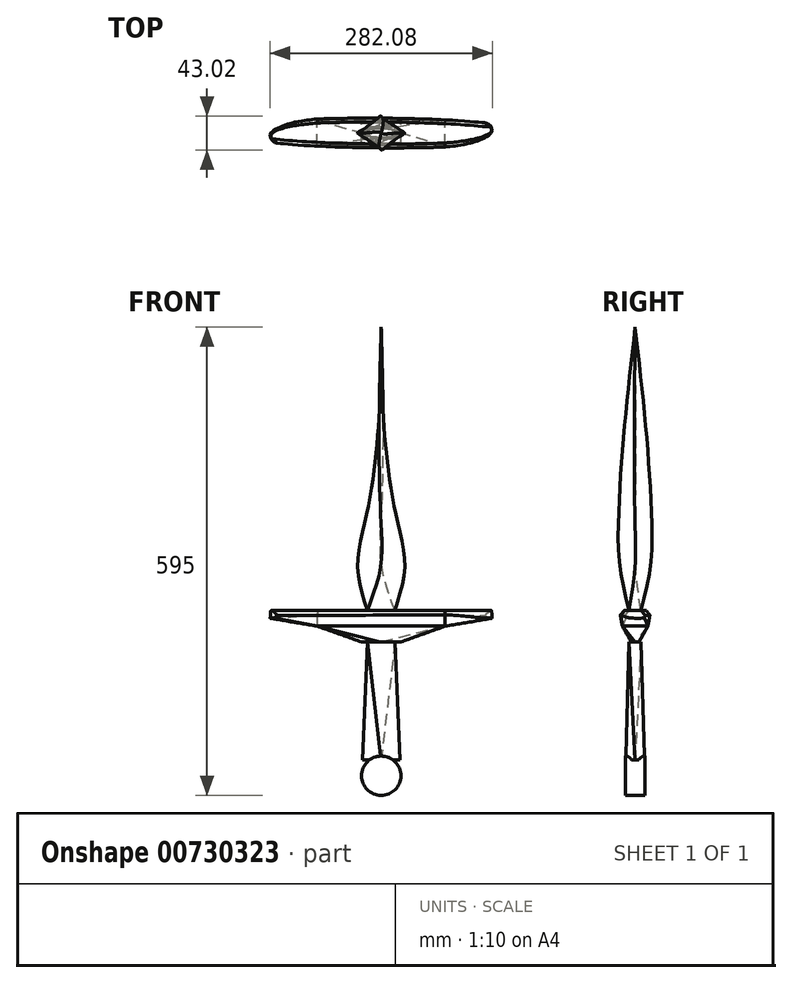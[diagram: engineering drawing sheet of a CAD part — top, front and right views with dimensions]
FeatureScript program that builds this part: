
annotation { "Feature Type Name" : "Feature", "Feature Type Description" : "" }
export const myFeature = defineFeature(function(context is Context, id is Id, definition is map)
    precondition{}
    {
        {
            var Q0;
            Q0=qCreatedBy(makeId("Top.planeOp"),FACE);
            cPlane(context, id + "F0", {"entities" : qUnion([Q0]), "cplaneType" : CPlaneType.OFFSET, "offset" : 57.5 * mm, "width" : 150 * mm, "height" : 150 * mm});
        }
        {
            var Q0;
            Q0=qCreatedBy(id+"F0.planeOp",FACE);
            cPlane(context, id + "F1", {"entities" : qUnion([Q0]), "cplaneType" : CPlaneType.OFFSET, "offset" : 2.5 * mm, "width" : 150 * mm, "height" : 150 * mm});
        }
        {
            var Q0;
            Q0=qCreatedBy(makeId("Top.planeOp"),FACE);
            cPlane(context, id + "F2", {"entities" : qUnion([Q0]), "cplaneType" : CPlaneType.OFFSET, "offset" : 20 * mm, "oppositeDirection" : true, "width" : 150 * mm, "height" : 150 * mm});
        }
        {
            var Q0;
            Q0=qCreatedBy(id+"F2.planeOp",FACE);
            cPlane(context, id + "F3", {"entities" : qUnion([Q0]), "cplaneType" : CPlaneType.OFFSET, "offset" : 20 * mm, "oppositeDirection" : true, "width" : 150 * mm, "height" : 150 * mm});
        }
        {
            var Q0;
            Q0=qCreatedBy(id+"F3.planeOp",FACE);
            cPlane(context, id + "F4", {"entities" : qUnion([Q0]), "cplaneType" : CPlaneType.OFFSET, "offset" : 150 * mm, "oppositeDirection" : true, "width" : 150 * mm, "height" : 150 * mm});
        }
        {
            var Q0;
            Q0=qCreatedBy(makeId("Top.planeOp"),FACE);
            cPlane(context, id + "F5", {"entities" : qUnion([Q0]), "cplaneType" : CPlaneType.OFFSET, "offset" : 400 * mm, "width" : 150 * mm, "height" : 150 * mm});
        }
        {
            var Q0;
            Q0=qCreatedBy(id+"F5.planeOp",FACE);
            cPlane(context, id + "F6", {"entities" : qUnion([Q0]), "cplaneType" : CPlaneType.OFFSET, "offset" : 40 * mm, "oppositeDirection" : true, "width" : 150 * mm, "height" : 150 * mm});
        }
        {
            var Q0;
            Q0=qCreatedBy(id+"F1.planeOp",FACE);
            cPlane(context, id + "F7", {"entities" : qUnion([Q0]), "cplaneType" : CPlaneType.OFFSET, "offset" : 50 * mm, "width" : 150 * mm, "height" : 150 * mm});
        }
        {
            var Q0;
            Q0=qCreatedBy(makeId("Top.planeOp"),FACE);
            var sketch = newSketch(context, id + "F8", { "sketchPlane" : qUnion([Q0])});
            skLineSegment(sketch, "E0.bottom", {"start": v(17.5, -7.5) * mm, "end": v(-17.5, -7.5) * mm});
            skLineSegment(sketch, "E0.top", {"start": v(17.5, 7.5) * mm, "end": v(-17.5, 7.5) * mm});
            skLineSegment(sketch, "E0.left", {"start": v(17.5, -7.5) * mm, "end": v(17.5, 7.5) * mm});
            skLineSegment(sketch, "E0.right", {"start": v(-17.5, -7.5) * mm, "end": v(-17.5, 7.5) * mm});
            skPoint(sketch, "E0.middle", {"position": v(0, 0) * mm});
            skSolve(sketch);
        }
        {
            var Q0;
            Q0=qCreatedBy(id+"F0.planeOp",FACE);
            var sketch = newSketch(context, id + "F9", { "sketchPlane" : qUnion([Q0])});
            skLineSegment(sketch, "E1", {"start": v(0, 0) * mm, "end": v(0, 16.67) * mm, "construction": true});
            skLineSegment(sketch, "E2", {"start": v(0, 16.67) * mm, "end": v(-25, 0) * mm});
            skLineSegment(sketch, "E3", {"start": v(-25, 0) * mm, "end": v(0, -16.67) * mm});
            skLineSegment(sketch, "E4", {"start": v(0, -16.67) * mm, "end": v(25, 0) * mm});
            skLineSegment(sketch, "E5", {"start": v(25, 0) * mm, "end": v(0, 16.67) * mm});
            skLineSegment(sketch, "E6", {"start": v(0, 0) * mm, "end": v(25, 0) * mm, "construction": true});
            skLineSegment(sketch, "E7.bottom", {"start": v(-12.5, -8.33) * mm, "end": v(12.5, -8.33) * mm});
            skLineSegment(sketch, "E7.top", {"start": v(-12.5, 8.33) * mm, "end": v(12.5, 8.33) * mm});
            skLineSegment(sketch, "E7.left", {"start": v(-12.5, -8.33) * mm, "end": v(-12.5, 8.33) * mm});
            skLineSegment(sketch, "E7.right", {"start": v(12.5, -8.33) * mm, "end": v(12.5, 8.33) * mm});
            skSolve(sketch);
        }
        {
            var Q0;
            Q0=qCreatedBy(id+"F1.planeOp",FACE);
            var sketch = newSketch(context, id + "F10", { "sketchPlane" : qUnion([Q0])});
            skLineSegment(sketch, "E8", {"start": v(0, 0) * mm, "end": v(0, 20) * mm, "construction": true});
            skLineSegment(sketch, "E9", {"start": v(0, 20) * mm, "end": v(30, 0) * mm});
            skLineSegment(sketch, "E10", {"start": v(30, 0) * mm, "end": v(0, -20) * mm});
            skLineSegment(sketch, "E11", {"start": v(0, -20) * mm, "end": v(-30, 0) * mm});
            skLineSegment(sketch, "E12", {"start": v(-30, 0) * mm, "end": v(0, 20) * mm});
            skLineSegment(sketch, "E13", {"start": v(0, 0) * mm, "end": v(-30, 0) * mm, "construction": true});
            skSolve(sketch);
        }
        {
            var Q0;
            Q0=qCreatedBy(makeId("Top.planeOp"),FACE);
            var sketch = newSketch(context, id + "F11", { "sketchPlane" : qUnion([Q0])});
            skPoint(sketch, "E14.middle", {"position": v(0, 0) * mm});
            skLineSegment(sketch, "E15", {"start": v(0, 0) * mm, "end": v(-200, 0) * mm, "construction": true});
            skEllipse(sketch, "E16", {"center": v(0, 0) * mm, "majorRadius": 200 * mm, "minorRadius": 20 * mm, "majorAxis": v(-1, 0)});
            skSolve(sketch);
        }
        {
            var Q0;
            Q0=qCreatedBy(id+"F2.planeOp",FACE);
            var sketch = newSketch(context, id + "F12", { "sketchPlane" : qUnion([Q0])});
            skLineSegment(sketch, "E17.bottom", {"start": v(81.25, -16.25) * mm, "end": v(-81.25, -16.25) * mm});
            skLineSegment(sketch, "E17.top", {"start": v(81.25, 16.25) * mm, "end": v(-81.25, 16.25) * mm});
            skLineSegment(sketch, "E17.left", {"start": v(81.25, -16.25) * mm, "end": v(81.25, 16.25) * mm});
            skLineSegment(sketch, "E17.right", {"start": v(-81.25, -16.25) * mm, "end": v(-81.25, 16.25) * mm});
            skPoint(sketch, "E17.middle", {"position": v(0, 0) * mm});
            skSolve(sketch);
        }
        {
            var Q0;
            Q0=qCreatedBy(id+"F3.planeOp",FACE);
            var sketch = newSketch(context, id + "F13", { "sketchPlane" : qUnion([Q0])});
            skPoint(sketch, "E18.middle", {"position": v(0, 0) * mm});
            skLineSegment(sketch, "E19", {"start": v(0, 0) * mm, "end": v(-25, 0) * mm, "construction": true});
            skEllipse(sketch, "E20", {"center": v(0, 0) * mm, "majorRadius": 25 * mm, "minorRadius": 5 * mm, "majorAxis": v(-1, 0)});
            skSolve(sketch);
        }
        {
            var Q0;
            Q0=qCreatedBy(makeId("Front.planeOp"),FACE);
            var sketch = newSketch(context, id + "F14", { "sketchPlane" : qUnion([Q0])});
            skLineSegment(sketch, "E21", {"start": v(0, 0) * mm, "end": v(0, -210) * mm, "construction": true});
            skCircle(sketch, "E22", {"center": v(0, -210) * mm, "radius": 25 * mm});
            skSolve(sketch);
        }
        {
            var Q0;
            Q0=qCreatedBy(id+"F3.planeOp",FACE);
            var sketch = newSketch(context, id + "F15", { "sketchPlane" : qUnion([Q0])});
            skLineSegment(sketch, "E23.bottom", {"start": v(17.5, -7.5) * mm, "end": v(-17.5, -7.5) * mm});
            skLineSegment(sketch, "E23.top", {"start": v(17.5, 7.5) * mm, "end": v(-17.5, 7.5) * mm});
            skLineSegment(sketch, "E23.left", {"start": v(17.5, -7.5) * mm, "end": v(17.5, 7.5) * mm});
            skLineSegment(sketch, "E23.right", {"start": v(-17.5, -7.5) * mm, "end": v(-17.5, 7.5) * mm});
            skPoint(sketch, "E23.middle", {"position": v(0, 0) * mm});
            skSolve(sketch);
        }
        {
            var Q0;
            Q0=qCreatedBy(id+"F6.planeOp",FACE);
            var sketch = newSketch(context, id + "F16", { "sketchPlane" : qUnion([Q0])});
            skLineSegment(sketch, "E24", {"start": v(0, 17.68) * mm, "end": v(17.68, 0) * mm});
            skLineSegment(sketch, "E25", {"start": v(17.68, 0) * mm, "end": v(0, -17.68) * mm});
            skLineSegment(sketch, "E26", {"start": v(0, -17.68) * mm, "end": v(-17.68, 0) * mm});
            skLineSegment(sketch, "E27", {"start": v(-17.68, 0) * mm, "end": v(0, 17.68) * mm});
            skLineSegment(sketch, "E28", {"start": v(-17.68, 0) * mm, "end": v(17.68, 0) * mm, "construction": true});
            skLineSegment(sketch, "E29", {"start": v(0, 17.68) * mm, "end": v(0, -17.68) * mm, "construction": true});
            skPoint(sketch, "E30", {"position": v(0, 0) * mm});
            skSolve(sketch);
        }
        {
            var Q0;
            Q0=qCreatedBy(id+"F4.planeOp",FACE);
            var sketch = newSketch(context, id + "F17", { "sketchPlane" : qUnion([Q0])});
            skLineSegment(sketch, "E31", {"start": v(0, 0) * mm, "end": v(0, -12) * mm, "construction": true});
            skLineSegment(sketch, "E32", {"start": v(0, -12) * mm, "end": v(-24, 0) * mm});
            skLineSegment(sketch, "E33", {"start": v(-24, 0) * mm, "end": v(0, 12) * mm});
            skLineSegment(sketch, "E34", {"start": v(0, 12) * mm, "end": v(24, 0) * mm});
            skLineSegment(sketch, "E35", {"start": v(24, 0) * mm, "end": v(0, -12) * mm});
            skLineSegment(sketch, "E36", {"start": v(0, 0) * mm, "end": v(24, 0) * mm, "construction": true});
            skSolve(sketch);
        }
        {
            var Q0;
            Q0=qCreatedBy(id+"F7.planeOp",FACE);
            var sketch = newSketch(context, id + "F18", { "sketchPlane" : qUnion([Q0])});
            skLineSegment(sketch, "E37.bottom", {"start": v(10.62, -10.62) * mm, "end": v(-10.62, -10.63) * mm, "construction": true});
            skLineSegment(sketch, "E37.top", {"start": v(10.62, 10.63) * mm, "end": v(-10.62, 10.62) * mm, "construction": true});
            skLineSegment(sketch, "E37.left", {"start": v(10.62, -10.62) * mm, "end": v(10.62, 10.63) * mm, "construction": true});
            skLineSegment(sketch, "E37.right", {"start": v(-10.62, -10.63) * mm, "end": v(-10.62, 10.62) * mm, "construction": true});
            skPoint(sketch, "E37.middle", {"position": v(0, 0) * mm});
            skLineSegment(sketch, "E38", {"start": v(-21.21, 0) * mm, "end": v(0, 21.21) * mm});
            skPoint(sketch, "E38.startSnap0", {"position": v(-10.62, 0) * mm});
            skLineSegment(sketch, "E39", {"start": v(0, 21.21) * mm, "end": v(21.21, 0) * mm});
            skLineSegment(sketch, "E40", {"start": v(21.21, 0) * mm, "end": v(0, -21.21) * mm});
            skLineSegment(sketch, "E41", {"start": v(0, -21.21) * mm, "end": v(-21.21, 0) * mm});
            skSolve(sketch);
        }
        {
            var Q0;
            Q0=makeQuery(id+"F11.imprint","IMPRINT",FACE,{"disambiguationData":[TD([[makeQuery(id+"F11.imprint","IMPRINT",EDGE,{"derivedFrom":sQuery(id+"F11.wireOp",EDGE,"E16")}),1.0]])]});
            var Q1;
            Q1=makeQuery(id+"F12.imprint","IMPRINT",FACE,{"disambiguationData":[TD([[makeQuery(id+"F12.imprint","IMPRINT",EDGE,{"derivedFrom":sQuery(id+"F12.wireOp",EDGE,"E17.bottom")}),-1.0]])]});
            loft(context, id + "F19", {"sheetProfilesArray" : [{ "sheetProfileEntities" : qUnion([Q0]) }, { "sheetProfileEntities" : qUnion([Q1]) }]});
        }
        {
            var Q1;
            Q1=makeQuery(id+"F12.imprint","IMPRINT",FACE,{"disambiguationData":[TD([[makeQuery(id+"F12.imprint","IMPRINT",EDGE,{"derivedFrom":sQuery(id+"F12.wireOp",EDGE,"E17.bottom")}),-1.0]])]});
            var Q2;
            Q2=makeQuery(id+"F13.imprint","IMPRINT",FACE,{"disambiguationData":[TD([[makeQuery(id+"F13.imprint","IMPRINT",EDGE,{"derivedFrom":sQuery(id+"F13.wireOp",EDGE,"E20")}),1.0]])]});
            loft(context, id + "F20", {"operationType" : NewBodyOperationType.ADD, "sheetProfilesArray" : [{ "sheetProfileEntities" : qUnion([Q1]) }, { "sheetProfileEntities" : qUnion([Q2]) }]});
        }
        {
            var Q1;
            Q1 = qSketchRegion(id + "F8", true);
            var Q2;
            Q2=makeQuery(id+"F10.imprint","IMPRINT",FACE,{"disambiguationData":[TD([[makeQuery(id+"F10.imprint","IMPRINT",EDGE,{"derivedFrom":sQuery(id+"F10.wireOp",EDGE,"E9")}),-1.0]])]});
            var Q3;
            Q3 = qSketchRegion(id + "F18", true);
            var Q4;
            Q4=sQuery(id+"F16.wireOp",VERTEX,"E30");
            var Q5;
            Q5 = qConstructionFilter(qBodyType(qCreatedBy(id + "F8" ,EDGE), BodyType.WIRE), ConstructionObject.NO);
            var Q6;
            Q6 = qConstructionFilter(qBodyType(qCreatedBy(id + "F9" ,EDGE), BodyType.WIRE), ConstructionObject.NO);
            var Q7;
            Q7 = qConstructionFilter(qBodyType(qCreatedBy(id + "F10" ,EDGE), BodyType.WIRE), ConstructionObject.NO);
            var Q8;
            Q8=sQuery(id+"F8.wireOp",VERTEX,"E0.middle");
            var Q9;
            Q9=sQuery(id+"F10.wireOp",VERTEX,"E8.start");
            var Q10;
            Q10=sQuery(id+"F18.wireOp",VERTEX,"E37.middle");
            var Q11;
            Q11=sQuery(id+"F16.wireOp",VERTEX,"0wCMpsBQ-amod-RNqf-wESM-xm9LtcAPylre.middle");
            loft(context, id + "F21", {"sheetProfilesArray" : [{ "sheetProfileEntities" : qUnion([Q1]) }, { "sheetProfileEntities" : qUnion([Q2]) }, { "sheetProfileEntities" : qUnion([Q3]) }, { "sheetProfileEntities" : qUnion([Q4]) }], "wireProfilesArray" : [{ "wireProfileEntities" : qUnion([Q5]) }, { "wireProfileEntities" : qUnion([Q6]) }, { "wireProfileEntities" : qUnion([Q7]) }], "connections" : [{ "connectionEntities" : qUnion([Q8, Q9, Q10, Q11]), "connectionEdgeQueries" : qUnion([]), "connectionEdgeParameters" : [] }]});
        }
        {
            var Q0;
            Q0=makeQuery(id+"F14.imprint","IMPRINT",FACE,{"disambiguationData":[TD([[makeQuery(id+"F14.imprint","IMPRINT",EDGE,{"derivedFrom":sQuery(id+"F14.wireOp",EDGE,"E22")}),1.0]])]});
            extrude(context, id + "F22", {"entities" : qUnion([Q0]), "operationType" : NewBodyOperationType.ADD, "endBound" : BoundingType.SYMMETRIC, "depth" : 25 * mm});
        }
        {
            var Q1;
            Q1=makeQuery(id+"F15.imprint","IMPRINT",FACE,{"disambiguationData":[TD([[makeQuery(id+"F15.imprint","IMPRINT",EDGE,{"derivedFrom":sQuery(id+"F15.wireOp",EDGE,"E23.bottom")}),-1.0]])]});
            var Q2;
            Q2=makeQuery(id+"F17.imprint","IMPRINT",FACE,{"disambiguationData":[TD([[makeQuery(id+"F17.imprint","IMPRINT",EDGE,{"derivedFrom":sQuery(id+"F17.wireOp",EDGE,"E32")}),-1.0]])]});
            loft(context, id + "F23", {"operationType" : NewBodyOperationType.ADD, "sheetProfilesArray" : [{ "sheetProfileEntities" : qUnion([Q1]) }, { "sheetProfileEntities" : qUnion([Q2]) }]});
        }
        {
            var Q0;
            Q0=makeQuery(id+"F19.opLoft","MID_CAP_EDGE",EDGE,{"disambiguationData":[OSD([sQuery(id+"F11.wireOp",EDGE,"E16"),sQuery(id+"F12.wireOp",EDGE,"E17.bottom"),sQuery(id+"F12.wireOp",EDGE,"E17.top"),sQuery(id+"F12.wireOp",EDGE,"E17.right")])],"capPos":0.0});
            var Q1;
            Q1=makeQuery(id+"F19.opLoft","MID_CAP_EDGE",EDGE,{"disambiguationData":[OSD([sQuery(id+"F11.wireOp",EDGE,"E16"),sQuery(id+"F12.wireOp",EDGE,"E17.bottom"),sQuery(id+"F12.wireOp",EDGE,"E17.top"),sQuery(id+"F12.wireOp",EDGE,"E17.left"),sQuery(id+"F12.wireOp",EDGE,"E17.right")])],"capPos":0.0});
            var Q2;
            Q2=makeQuery(id+"F19.opLoft","MID_CAP_EDGE",EDGE,{"disambiguationData":[OSD([sQuery(id+"F11.wireOp",EDGE,"E16"),sQuery(id+"F12.wireOp",EDGE,"E17.bottom"),sQuery(id+"F12.wireOp",EDGE,"E17.left")])],"capPos":0.0});
            var Q3;
            Q3=makeQuery(id+"F19.opLoft","MID_CAP_EDGE",EDGE,{"disambiguationData":[OSD([sQuery(id+"F11.wireOp",EDGE,"E16"),sQuery(id+"F12.wireOp",EDGE,"E17.bottom"),sQuery(id+"F12.wireOp",EDGE,"E17.left"),sQuery(id+"F12.wireOp",EDGE,"E17.right")])],"capPos":0.0});
            chamfer(context, id + "F24", {"entities" : qUnion([Q0, Q1, Q2, Q3]), "width" : 5 * mm, "tangentPropagation" : true});
        }
    });
